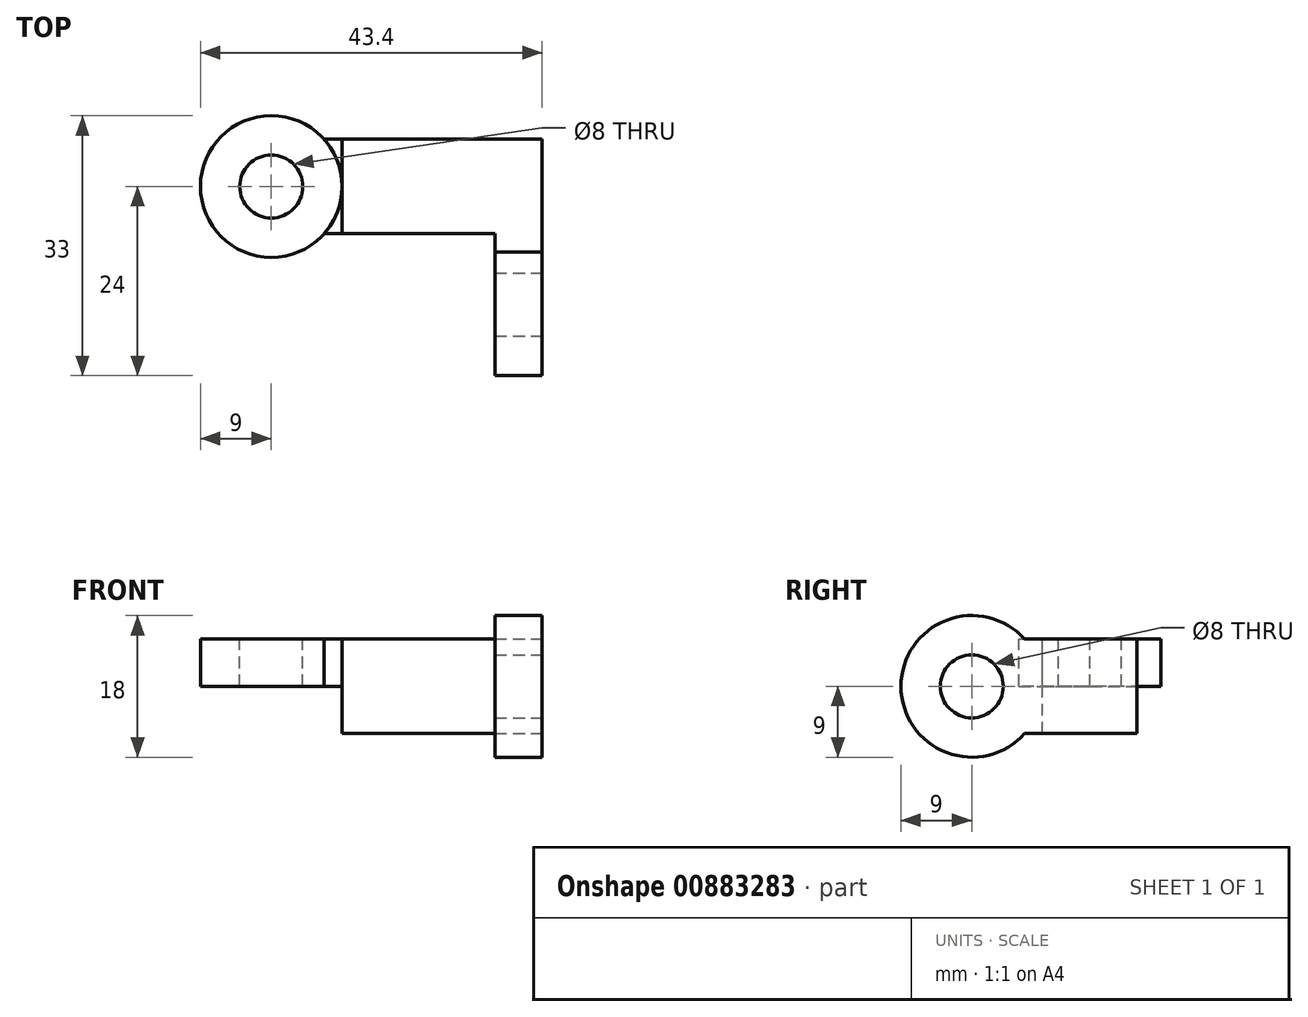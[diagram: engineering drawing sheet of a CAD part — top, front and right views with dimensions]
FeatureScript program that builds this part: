
annotation { "Feature Type Name" : "Feature", "Feature Type Description" : "" }
export const myFeature = defineFeature(function(context is Context, id is Id, definition is map)
    precondition{}
    {
        {
            var Q0;
            Q0=qCreatedBy(makeId("Top.planeOp"),FACE);
            var sketch = newSketch(context, id + "F0", { "sketchPlane" : qUnion([Q0])});
            skLineSegment(sketch, "E0", {"start": v(0, 0) * mm, "end": v(-12.7, 0) * mm});
            skCircle(sketch, "E1", {"center": v(-21.7, 0) * mm, "radius": 4 * mm});
            skLineSegment(sketch, "E2", {"start": v(0, 0) * mm, "end": v(12.7, 0) * mm});
            skLineSegment(sketch, "E3", {"start": v(0, 0) * mm, "end": v(0, 6) * mm});
            skLineSegment(sketch, "E4", {"start": v(0, 6) * mm, "end": v(0, -6) * mm});
            skLineSegment(sketch, "E5", {"start": v(0, -6) * mm, "end": v(-12.7, -6) * mm});
            skLineSegment(sketch, "E6", {"start": v(0, 6) * mm, "end": v(-12.7, 6) * mm});
            skLineSegment(sketch, "E7", {"start": v(0, 6) * mm, "end": v(12.7, 6) * mm});
            skLineSegment(sketch, "E8", {"start": v(12.7, 6) * mm, "end": v(12.7, -6) * mm});
            skLineSegment(sketch, "E9", {"start": v(12.7, -6) * mm, "end": v(0, -6) * mm});
            skLineSegment(sketch, "E10", {"start": v(12.7, -6) * mm, "end": v(7.7, -6) * mm});
            skLineSegment(sketch, "E11", {"start": v(7.7, -6) * mm, "end": v(7.7, -24) * mm});
            skLineSegment(sketch, "E12", {"start": v(7.7, -24) * mm, "end": v(12.7, -24) * mm});
            skLineSegment(sketch, "E13", {"start": v(12.7, -24) * mm, "end": v(12.7, -6) * mm});
            skCircle(sketch, "E14", {"center": v(-21.7, 0) * mm, "radius": 9 * mm});
            skLineSegment(sketch, "E15", {"start": v(-12.7, 6) * mm, "end": v(-15, 6) * mm});
            skLineSegment(sketch, "E16", {"start": v(-12.7, -6) * mm, "end": v(-15, -6) * mm});
            skLineSegment(sketch, "E17", {"start": v(-12.7, 0) * mm, "end": v(-12.7, 6) * mm});
            skLineSegment(sketch, "E18", {"start": v(-12.7, 0) * mm, "end": v(-12.7, -6) * mm});
            skSolve(sketch);
        }
        {
            var Q0;
            Q0=makeQuery(id+"F0.imprint","IMPRINT",FACE,{"disambiguationData":[TD([[makeQuery(id+"F0.imprint","IMPRINT",EDGE,{"derivedFrom":sQuery(id+"F0.wireOp",EDGE,"E1")}),-1.0]])]});
            extrude(context, id + "F1", {"entities" : qUnion([Q0]), "oppositeDirection" : true, "depth" : 6 * mm, "offsetDistance" : 25 * mm});
        }
        {
            var Q0;
            Q0=makeQuery(id+"F0.imprint","IMPRINT",FACE,{"disambiguationData":[TD([[makeQuery(id+"F0.imprint","IMPRINT",EDGE,{"derivedFrom":sQuery(id+"F0.wireOp",EDGE,"E0")}),-1.0]])]});
            var Q1;
            {var subQ0=sQuery(id+"F0.wireOp",EDGE,"E2");Q1=makeQuery(id+"F0.imprint","IMPRINT",FACE,{"disambiguationData":[TD([[makeQuery(id+"F0.imprint","IMPRINT",EDGE,{"derivedFrom":subQ0}),1.0]])]});}
            var Q2;
            Q2=makeQuery(id+"F0.imprint","IMPRINT",FACE,{"disambiguationData":[TD([[makeQuery(id+"F0.imprint","IMPRINT",EDGE,{"derivedFrom":sQuery(id+"F0.wireOp",EDGE,"E0")}),1.0]])]});
            var Q3;
            {var subQ4=sQuery(id+"F0.wireOp",EDGE,"E2");Q3=makeQuery(id+"F0.imprint","IMPRINT",FACE,{"disambiguationData":[TD([[makeQuery(id+"F0.imprint","IMPRINT",EDGE,{"derivedFrom":subQ4}),-1.0]])]});}
            extrude(context, id + "F2", {"entities" : qUnion([Q0, Q1, Q2, Q3]), "operationType" : NewBodyOperationType.ADD, "oppositeDirection" : true, "depth" : 12 * mm, "offsetDistance" : 25 * mm});
        }
        {
            var Q0;
            {var subQ2=sQuery(id+"F0.wireOp",EDGE,"E15");Q0=makeQuery(id+"F0.imprint","IMPRINT",FACE,{"disambiguationData":[TD([[makeQuery(id+"F0.imprint","IMPRINT",EDGE,{"derivedFrom":subQ2}),1.0]])]});}
            var Q1;
            {var subQ2=sQuery(id+"F0.wireOp",EDGE,"E16");Q1=makeQuery(id+"F0.imprint","IMPRINT",FACE,{"disambiguationData":[TD([[makeQuery(id+"F0.imprint","IMPRINT",EDGE,{"derivedFrom":subQ2}),-1.0]])]});}
            extrude(context, id + "F3", {"entities" : qUnion([Q0, Q1]), "oppositeDirection" : true, "depth" : 6 * mm, "offsetDistance" : 25 * mm});
        }
        {
            var Q0;
            Q0=makeQuery(id+"F2.opExtrude","SWEPT_FACE",FACE,{"disambiguationData":[OSD([sQuery(id+"F0.wireOp",EDGE,"E8")])]});
            var sketch = newSketch(context, id + "F4", { "sketchPlane" : qUnion([Q0])});
            skLineSegment(sketch, "E19", {"start": v(0, 0) * mm, "end": v(0, -6) * mm});
            skLineSegment(sketch, "E20", {"start": v(0, -6) * mm, "end": v(-6, -6) * mm});
            skLineSegment(sketch, "E21", {"start": v(-6, -6) * mm, "end": v(-15, -6) * mm});
            skCircle(sketch, "E22", {"center": v(-15, -6) * mm, "radius": 9 * mm});
            skLineSegment(sketch, "E23", {"start": v(-6, 0) * mm, "end": v(-8.3, 0) * mm});
            skLineSegment(sketch, "E24", {"start": v(-6, 0) * mm, "end": v(-6, -12) * mm});
            skLineSegment(sketch, "E25", {"start": v(-6, -12) * mm, "end": v(-8.3, -12) * mm});
            skSolve(sketch);
        }
        {
            var Q0;
            {var subQ0=sQuery(id+"F4.wireOp",EDGE,"E22");var subQ2=makeQuery(id+"F4.imprint","INTERSECT",VERTEX,{"derivedFrom":[subQ0,sQuery(id+"F4.wireOp",EDGE,"E23")]});Q0=makeQuery(id+"F4.imprint","IMPRINT",FACE,{"disambiguationData":[TD([[makeQuery(id+"F4.imprint","IMPRINT",EDGE,{"disambiguationData":[TD([[subQ2,-1.0]])],"derivedFrom":subQ0}),1.0]])]});}
            var Q1;
            {var subQ3=sQuery(id+"F4.wireOp",EDGE,"E25");Q1=makeQuery(id+"F4.imprint","IMPRINT",FACE,{"disambiguationData":[TD([[makeQuery(id+"F4.imprint","IMPRINT",EDGE,{"derivedFrom":subQ3}),-1.0]])]});}
            var Q2;
            {var subQ3=sQuery(id+"F4.wireOp",EDGE,"E23");Q2=makeQuery(id+"F4.imprint","IMPRINT",FACE,{"disambiguationData":[TD([[makeQuery(id+"F4.imprint","IMPRINT",EDGE,{"derivedFrom":subQ3}),1.0]])]});}
            extrude(context, id + "F5", {"entities" : qUnion([Q0, Q1, Q2]), "operationType" : NewBodyOperationType.ADD, "oppositeDirection" : true, "depth" : 6 * mm, "offsetDistance" : 25 * mm});
        }
        {
            var Q0;
            Q0=sQuery(id+"F4.wireOp",VERTEX,"E21.end");
            var Q1;
            Q1=makeQuery(id+"F2.opExtrude","SWEPT_BODY",BODY,{"disambiguationData":[OSD([sQuery(id+"F0.wireOp",EDGE,"E5"),sQuery(id+"F0.wireOp",EDGE,"E6"),sQuery(id+"F0.wireOp",EDGE,"E7"),sQuery(id+"F0.wireOp",EDGE,"E8"),sQuery(id+"F0.wireOp",EDGE,"E9"),sQuery(id+"F0.wireOp",EDGE,"E17"),sQuery(id+"F0.wireOp",EDGE,"E18")])]});
            hole(context, id + "F6", {"style" : HoleStyle.SIMPLE, "endStyle" : HoleEndStyle.THROUGH, "holeDiameter" : 8 * mm, "majorDiameter" : 5 * mm, "isTappedThrough" : true, "tappedDepth" : 12 * mm, "tapClearance" : 3, "locations" : qUnion([Q0]), "scope" : qUnion([Q1])});
        }
    });
